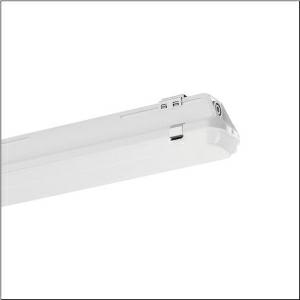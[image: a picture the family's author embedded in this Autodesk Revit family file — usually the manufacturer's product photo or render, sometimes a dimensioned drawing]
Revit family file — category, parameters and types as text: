
# Revit family: monsun_r__21_51fb207l420k_f7be
name_source: partatom
category: Lighting Fixtures
units: mm (PartAtom-declared; Revit-internal decimal feet)

## family parameters
Cut with Voids When Loaded = No
Host = Face
Light Source = No
Part Type = Normal
Room Calculation Point = No
Round Connector Dimension = Use Diameter
Shared = No

## types (1)
- Monsun® 21 (1 x LED, 2620 lm, 17.1 W, 4000K)
    Apparent Load = 17 VA
    CIE Flux Codes = 45 75 93 94 100
    Color Rendering = 80
    Color Temperature = 4000K
    Default Elevation = 1800 mm
    Description = Monsun® 21, damp-proof luminaire, chain hanger, primary optical cover: enclosure, of PC, light emission: direct distribution, primary light characteristic: symmetric, installation type: suspended mounting, surface-mounted, horizontal mounting, vertical mounting, LED, rated luminous flux: 2.620lm, luminous efficacy: 153lm/W, light colour: 840, colour temperature: 4000K, control gear: ON/OFF, with terminal, 3-pole, max. 2.5mm², mains connection: 220..240V, AC, 50/60Hz, rated input power: 17W, housing, of glass-fibre reinforced plastic, uncoated, bright grey, incl. chain hanger, length: 1.299mm, width: 90mm, height: 88mm, clip for enclosure, of stainless steel (V2A), ceiling mounting element, of stainless steel (V2A), chain hanger, of stainless steel (V2A), protection rating (complete): IP66, insulation class (complete): insulation class I (protective earthing), certification: CE, ENEC, VDE, UKCA, protection symbol: D, impact resistance: IK08, permissible operating ambient temperature: -25..+35°C, standard: EN 50419, EN 60598-2-1, corresponds to IFS (International Featured Standards) requirements for safety and quality in the food industry, for indoor or canopied outdoor use, no direct snow, no direct sun, no direct rain, LABS conformity tested according to VDMA 24364:2018-05, contact your sales advisor before using the luminaires in applications with unclear chemical exposure, large temperature fluctuations or condensation-forming humidity, packaging unit: 1 piece
    Height = 88 mm
    Lamp = 1 x LED
    Lamp Light Flux = 2620 lm
    Lamp Power = 17.1 W
    Lamp count = 1
    Length = 1299 mm
    Luminous efficacy = 153 lm/W
    Manufacturer = Siteco
    ModVariant = No
    Model = 51FB207L420K
    Mounting Place = Ceiling
    Mounting Type = Surface mounted
    Number of Poles = 1
    OnlyDefault = Yes
    Power Factor = 1
    Product Name = Monsun® 21
    Product group = damp-proof luminaire
    ProductGroupID = 301
    Protection Class = Protection class I
    Protection Degree = IP 66
    RLX_Detail_Level = 1
    RLX_Emergency_Light_Flux = 0 lm
    RLX_Emergency_Type = 0
    RLX_Emergency_Type_DB = No
    RlxData = <blob elided: 89809 chars, md5=7272e0a6>
    Socket = socket
    Standby Power = 0 W
    System Light Flux = 2620 lm
    System Power = 17 W
    Type Comments = Product without accessories
    Type Image = l_1319656.jpg
    URL = http://relux.com
    VarID = ---
    Voltage = 0 V
    Weight = 0.00 kg
    Width = 90 mm

## geometry (parser evidence)
native form markers: Blend x4, Sweep x13
no freeform markers — native parametric forms only
